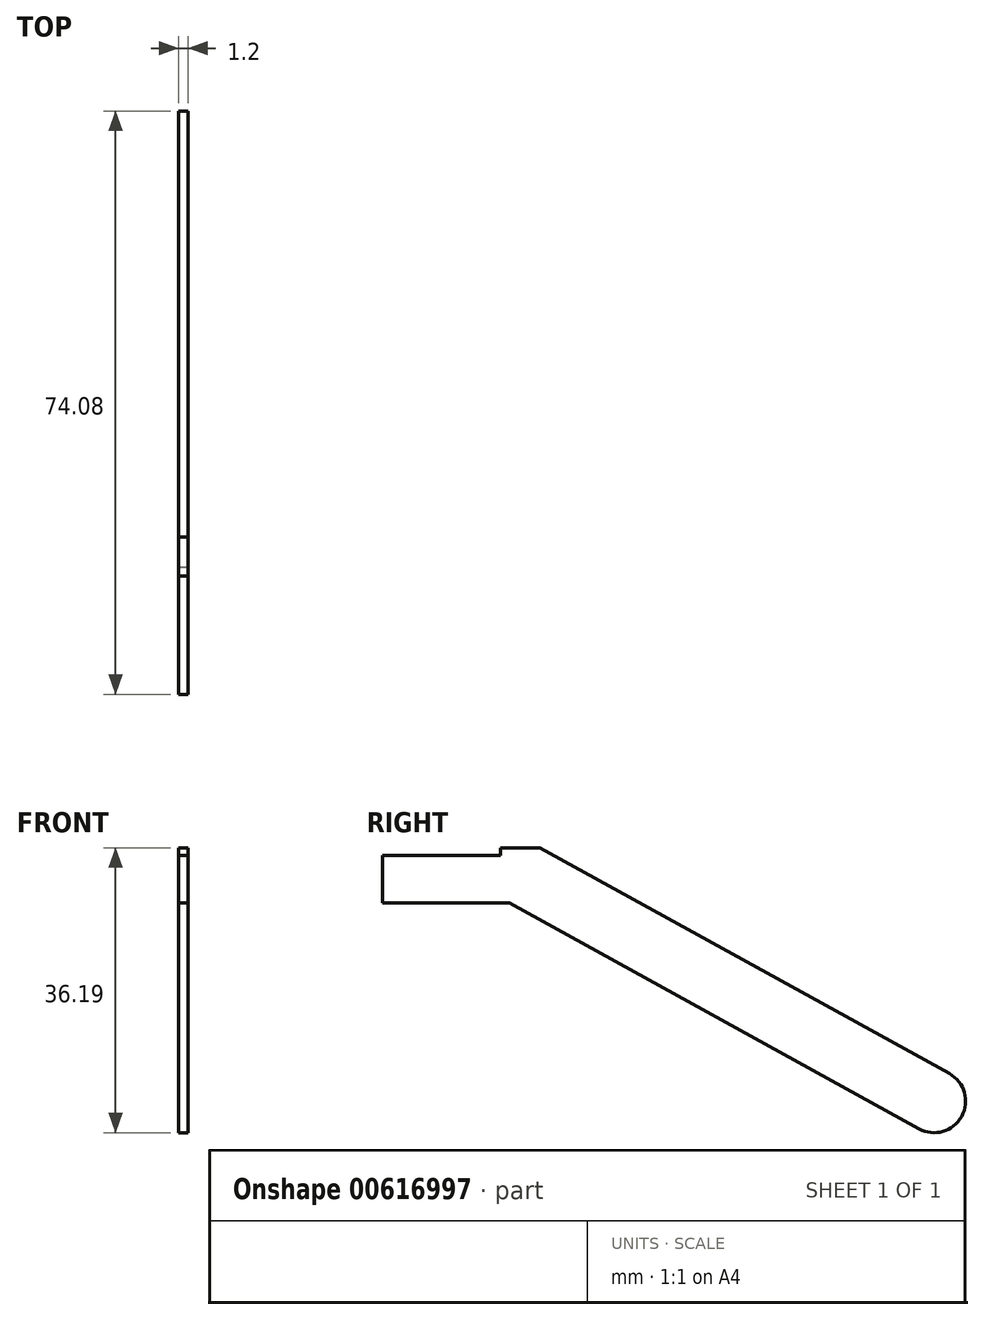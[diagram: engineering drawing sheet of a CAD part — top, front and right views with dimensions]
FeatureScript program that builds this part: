
annotation { "Feature Type Name" : "Feature", "Feature Type Description" : "" }
export const myFeature = defineFeature(function(context is Context, id is Id, definition is map)
    precondition{}
    {
        {
            var Q0;
            Q0=qCreatedBy(makeId("Right.planeOp"),FACE);
            var sketch = newSketch(context, id + "F0", { "sketchPlane" : qUnion([Q0])});
            skLineSegment(sketch, "E0", {"start": v(-70.08, 31.19) * mm, "end": v(-55.08, 31.19) * mm});
            skLineSegment(sketch, "E1", {"start": v(-55.08, 31.19) * mm, "end": v(-55.08, 32.19) * mm});
            skLineSegment(sketch, "E2", {"start": v(-55.08, 32.19) * mm, "end": v(-50.08, 32.19) * mm});
            skLineSegment(sketch, "E3", {"start": v(-50.08, 32.19) * mm, "end": v(1.93, 3.5) * mm});
            skArc(sketch, "E4", {"start": v(-1.93, -3.5) * mm, "mid": v(3.5, -1.93) * mm, "end": v(1.93, 3.5) * mm});
            skLineSegment(sketch, "E5", {"start": v(-70.08, 31.19) * mm, "end": v(-70.08, 25.19) * mm});
            skLineSegment(sketch, "E6", {"start": v(-70.08, 25.19) * mm, "end": v(-53.96, 25.19) * mm});
            skLineSegment(sketch, "E7", {"start": v(-53.96, 25.19) * mm, "end": v(-1.93, -3.5) * mm});
            skSolve(sketch);
        }
        {
            var Q0;
            Q0=makeQuery(id+"F0.imprint","IMPRINT",FACE,{"disambiguationData":[TD([[makeQuery(id+"F0.imprint","IMPRINT",EDGE,{"derivedFrom":sQuery(id+"F0.wireOp",EDGE,"E0")}),-1.0]])]});
            extrude(context, id + "F1", {"entities" : qUnion([Q0]), "endBound" : BoundingType.SYMMETRIC, "depth" : 1.2 * mm, "offsetDistance" : 25 * mm});
        }
    });
